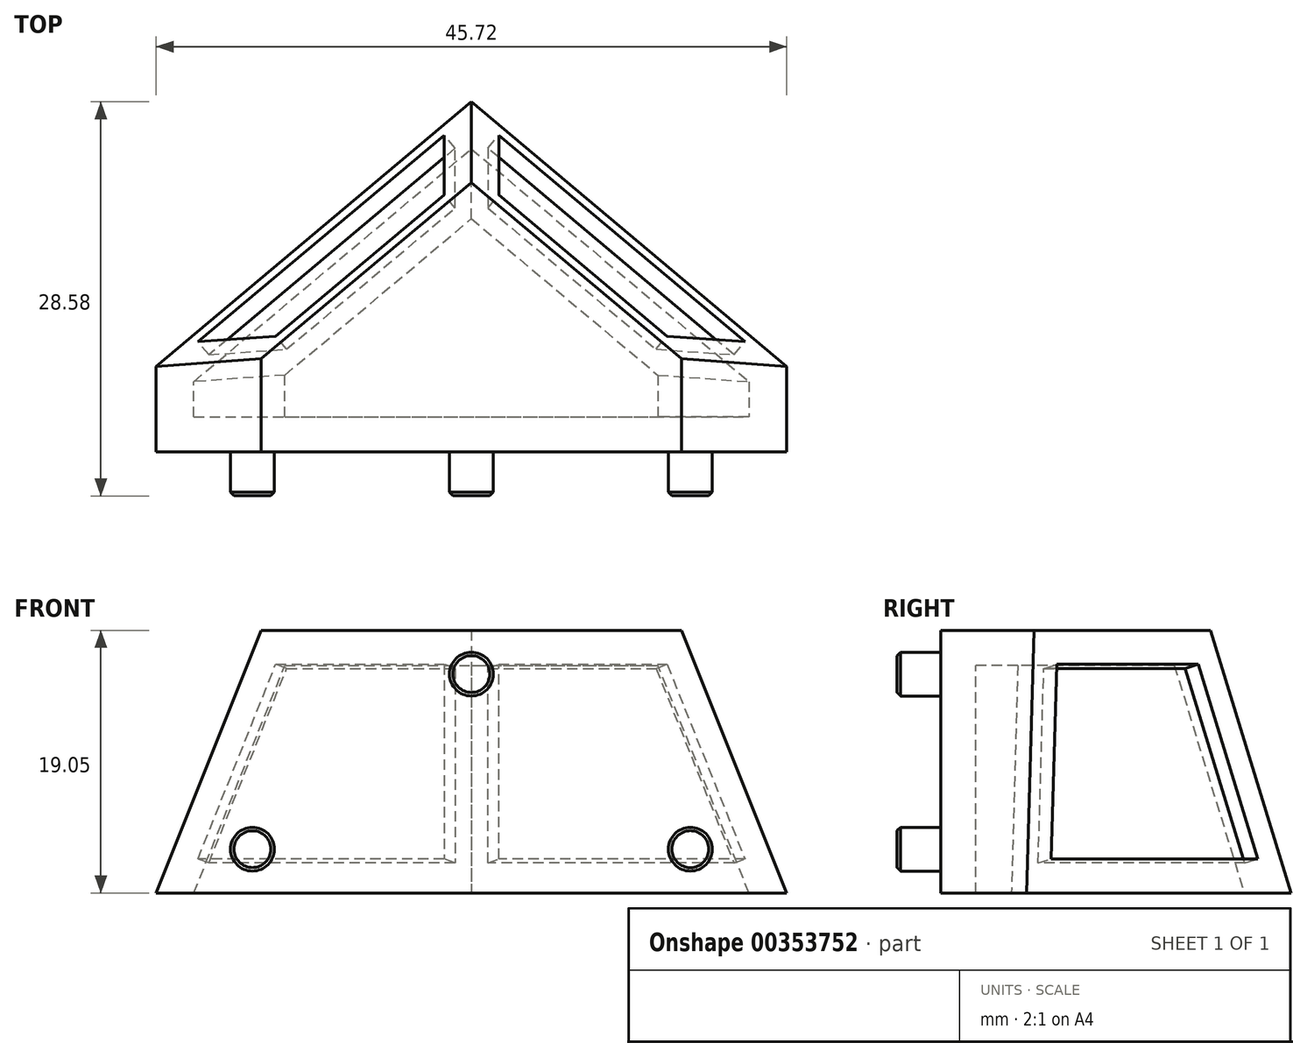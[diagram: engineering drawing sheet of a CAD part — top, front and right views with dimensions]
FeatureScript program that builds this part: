
annotation { "Feature Type Name" : "Feature", "Feature Type Description" : "" }
export const myFeature = defineFeature(function(context is Context, id is Id, definition is map)
    precondition{}
    {
        {
            var Q0;
            Q0=qCreatedBy(makeId("Top.planeOp"),FACE);
            var sketch = newSketch(context, id + "F0", { "sketchPlane" : qUnion([Q0])});
            skLineSegment(sketch, "E0", {"start": v(0, 0) * mm, "end": v(-22.86, 0) * mm});
            skLineSegment(sketch, "E1.MirrorCS", {"start": v(0, 0) * mm, "end": v(22.86, 0) * mm});
            skLineSegment(sketch, "E2", {"start": v(-22.86, 0) * mm, "end": v(-22.86, 6.22) * mm});
            skLineSegment(sketch, "E3", {"start": v(-22.86, 6.22) * mm, "end": v(0, 25.4) * mm});
            skLineSegment(sketch, "E4", {"start": v(0, 25.4) * mm, "end": v(22.86, 6.22) * mm});
            skLineSegment(sketch, "E5", {"start": v(22.86, 6.22) * mm, "end": v(22.86, 0) * mm});
            skSolve(sketch);
        }
        {
            var Q0;
            Q0=qCreatedBy(makeId("Top.planeOp"),FACE);
            cPlane(context, id + "F1", {"entities" : qUnion([Q0]), "cplaneType" : CPlaneType.OFFSET, "offset" : 19.05 * mm, "width" : 152.4 * mm, "height" : 152.4 * mm});
        }
        {
            var Q0;
            Q0=qCreatedBy(id+"F1.planeOp",FACE);
            var sketch = newSketch(context, id + "F2", { "sketchPlane" : qUnion([Q0])});
            skLineSegment(sketch, "E6", {"start": v(0, 0) * mm, "end": v(15.24, 0) * mm});
            skLineSegment(sketch, "E7.MirrorCS", {"start": v(0, 0) * mm, "end": v(-15.24, 0) * mm});
            skLineSegment(sketch, "E8", {"start": v(-15.24, 0) * mm, "end": v(-15.24, 6.76) * mm});
            skLineSegment(sketch, "E9", {"start": v(-15.24, 6.76) * mm, "end": v(0, 19.55) * mm});
            skLineSegment(sketch, "E10", {"start": v(0, 19.55) * mm, "end": v(15.24, 6.76) * mm});
            skLineSegment(sketch, "E11", {"start": v(15.24, 6.76) * mm, "end": v(15.24, 0) * mm});
            skSolve(sketch);
        }
        {
            var Q0;
            Q0=makeQuery(id+"F2.imprint","IMPRINT",FACE,{"disambiguationData":[TD([[makeQuery(id+"F2.imprint","IMPRINT",EDGE,{"derivedFrom":sQuery(id+"F2.wireOp",EDGE,"E6")}),1.0]])]});
            var Q1;
            Q1=makeQuery(id+"F0.imprint","IMPRINT",FACE,{"disambiguationData":[TD([[makeQuery(id+"F0.imprint","IMPRINT",EDGE,{"derivedFrom":sQuery(id+"F0.wireOp",EDGE,"E0")}),-1.0]])]});
            loft(context, id + "F3", {"sheetProfilesArray" : [{ "sheetProfileEntities" : qUnion([Q0]) }, { "sheetProfileEntities" : qUnion([Q1]) }]});
        }
        {
            var Q0;
            Q0=makeQuery(id+"F3.opLoft","CAP_FACE",FACE,{"disambiguationData":[OSD([makeQuery(id+"F0.imprint","IMPRINT",FACE,{"disambiguationData":[TD([[makeQuery(id+"F0.imprint","IMPRINT",EDGE,{"derivedFrom":sQuery(id+"F0.wireOp",EDGE,"E0")}),-1.0]])]})])],"isStart":true});
            shell(context, id + "F4", {"entities" : qUnion([Q0]), "thickness" : 2.54 * mm});
        }
        {
            var Q0;
            Q0=makeQuery(id+"F3.opLoft","SWEPT_FACE",FACE,{"disambiguationData":[OSD([sQuery(id+"F0.wireOp",EDGE,"E2"),sQuery(id+"F0.wireOp",EDGE,"E3"),sQuery(id+"F0.wireOp",EDGE,"E4"),sQuery(id+"F2.wireOp",EDGE,"E8"),sQuery(id+"F2.wireOp",EDGE,"E9"),sQuery(id+"F2.wireOp",EDGE,"E10")])]});
            var sketch = newSketch(context, id + "F5", { "sketchPlane" : qUnion([Q0])});
            skLineSegment(sketch, "E12.0", {"start": v(-12.65, 10.37) * mm, "end": v(-12.65, -4.38) * mm});
            skLineSegment(sketch, "E12.1", {"start": v(3, 13.38) * mm, "end": v(-12.65, 10.37) * mm});
            skLineSegment(sketch, "E12.2", {"start": v(10.23, 0.01) * mm, "end": v(3, 13.38) * mm});
            skLineSegment(sketch, "E12.3", {"start": v(-12.65, -4.38) * mm, "end": v(10.23, 0.01) * mm});
            skSolve(sketch);
        }
        {
            var Q0;
            Q0=makeQuery(id+"F5.imprint","IMPRINT",FACE,{"disambiguationData":[TD([[makeQuery(id+"F5.imprint","IMPRINT",EDGE,{"derivedFrom":sQuery(id+"F5.wireOp",EDGE,"E12.0")}),1.0]])]});
            extrude(context, id + "F6", {"entities" : qUnion([Q0]), "operationType" : NewBodyOperationType.REMOVE, "oppositeDirection" : true, "depth" : 1.27 * mm});
        }
        {
            var Q0;
            Q0=makeQuery(id+"F3.opLoft","SWEPT_FACE",FACE,{"disambiguationData":[OSD([sQuery(id+"F0.wireOp",EDGE,"E3"),sQuery(id+"F0.wireOp",EDGE,"E4"),sQuery(id+"F0.wireOp",EDGE,"E5"),sQuery(id+"F2.wireOp",EDGE,"E9"),sQuery(id+"F2.wireOp",EDGE,"E10"),sQuery(id+"F2.wireOp",EDGE,"E11")])]});
            var sketch = newSketch(context, id + "F7", { "sketchPlane" : qUnion([Q0])});
            skLineSegment(sketch, "E13.0", {"start": v(-3, 13.38) * mm, "end": v(-10.23, 0.01) * mm});
            skLineSegment(sketch, "E13.1", {"start": v(12.65, 10.37) * mm, "end": v(-3, 13.38) * mm});
            skLineSegment(sketch, "E13.2", {"start": v(12.65, -4.38) * mm, "end": v(12.65, 10.37) * mm});
            skLineSegment(sketch, "E13.3", {"start": v(-10.23, 0.01) * mm, "end": v(12.65, -4.38) * mm});
            skSolve(sketch);
        }
        {
            var Q0;
            Q0=makeQuery(id+"F7.imprint","IMPRINT",FACE,{"disambiguationData":[TD([[makeQuery(id+"F7.imprint","IMPRINT",EDGE,{"derivedFrom":sQuery(id+"F7.wireOp",EDGE,"E13.0")}),1.0]])]});
            extrude(context, id + "F8", {"entities" : qUnion([Q0]), "operationType" : NewBodyOperationType.REMOVE, "oppositeDirection" : true, "depth" : 1.27 * mm});
        }
        {
            var Q0;
            Q0=makeQuery(id+"F3.opLoft","SWEPT_FACE",FACE,{"disambiguationData":[OSD([sQuery(id+"F0.wireOp",EDGE,"E0"),sQuery(id+"F0.wireOp",EDGE,"E1.MirrorCS"),sQuery(id+"F0.wireOp",EDGE,"E5"),sQuery(id+"F2.wireOp",EDGE,"E6"),sQuery(id+"F2.wireOp",EDGE,"E7.MirrorCS"),sQuery(id+"F2.wireOp",EDGE,"E11")])]});
            var sketch = newSketch(context, id + "F9", { "sketchPlane" : qUnion([Q0])});
            skCircle(sketch, "E14", {"center": v(0, 15.88) * mm, "radius": 1.59 * mm});
            skCircle(sketch, "E15", {"center": v(15.88, 3.18) * mm, "radius": 1.59 * mm});
            skCircle(sketch, "E16", {"center": v(-15.88, 3.18) * mm, "radius": 1.59 * mm});
            skSolve(sketch);
        }
        {
            var Q0;
            Q0=makeQuery(id+"F9.imprint","IMPRINT",FACE,{"disambiguationData":[TD([[makeQuery(id+"F9.imprint","IMPRINT",EDGE,{"derivedFrom":sQuery(id+"F9.wireOp",EDGE,"E16")}),1.0]])]});
            var Q1;
            Q1=makeQuery(id+"F9.imprint","IMPRINT",FACE,{"disambiguationData":[TD([[makeQuery(id+"F9.imprint","IMPRINT",EDGE,{"derivedFrom":sQuery(id+"F9.wireOp",EDGE,"E14")}),1.0]])]});
            var Q2;
            Q2=makeQuery(id+"F9.imprint","IMPRINT",FACE,{"disambiguationData":[TD([[makeQuery(id+"F9.imprint","IMPRINT",EDGE,{"derivedFrom":sQuery(id+"F9.wireOp",EDGE,"E15")}),1.0]])]});
            extrude(context, id + "F10", {"entities" : qUnion([Q0, Q1, Q2]), "operationType" : NewBodyOperationType.ADD, "depth" : 2.92 * mm});
        }
        {
            var Q0;
            Q0=makeQuery(id+"F10.opExtrude","CAP_FACE",FACE,{"disambiguationData":[OSD([sQuery(id+"F9.wireOp",EDGE,"E14")])],"isStart":false});
            var sketch = newSketch(context, id + "F11", { "sketchPlane" : qUnion([Q0])});
            skCircle(sketch, "E17", {"center": v(0, 15.88) * mm, "radius": 1.59 * mm});
            skSolve(sketch);
        }
        {
            var Q0;
            Q0 = qSketchRegion(id + "F11", true);
            extrude(context, id + "F12", {"entities" : qUnion([Q0]), "operationType" : NewBodyOperationType.ADD, "depth" : 0.25 * mm, "hasDraft" : true, "draftAngle" : 45 * degree, "draftPullDirection" : true});
        }
        {
            var Q0;
            Q0=makeQuery(id+"F10.opExtrude","CAP_FACE",FACE,{"disambiguationData":[OSD([sQuery(id+"F9.wireOp",EDGE,"E15")])],"isStart":false});
            var sketch = newSketch(context, id + "F13", { "sketchPlane" : qUnion([Q0])});
            skCircle(sketch, "E18", {"center": v(15.88, 3.18) * mm, "radius": 1.6 * mm});
            skSolve(sketch);
        }
        {
            var Q0;
            Q0=makeQuery(id+"F10.opExtrude","CAP_FACE",FACE,{"disambiguationData":[OSD([sQuery(id+"F9.wireOp",EDGE,"E16")])],"isStart":false});
            var sketch = newSketch(context, id + "F14", { "sketchPlane" : qUnion([Q0])});
            skCircle(sketch, "E19", {"center": v(-15.88, 3.18) * mm, "radius": 1.59 * mm});
            skSolve(sketch);
        }
        {
            var Q0;
            Q0 = qSketchRegion(id + "F13", true);
            var Q1;
            Q1 = qSketchRegion(id + "F14", true);
            extrude(context, id + "F15", {"entities" : qUnion([Q0, Q1]), "operationType" : NewBodyOperationType.ADD, "depth" : 0.25 * mm, "hasDraft" : true, "draftAngle" : 45 * degree, "draftPullDirection" : true});
        }
    });
